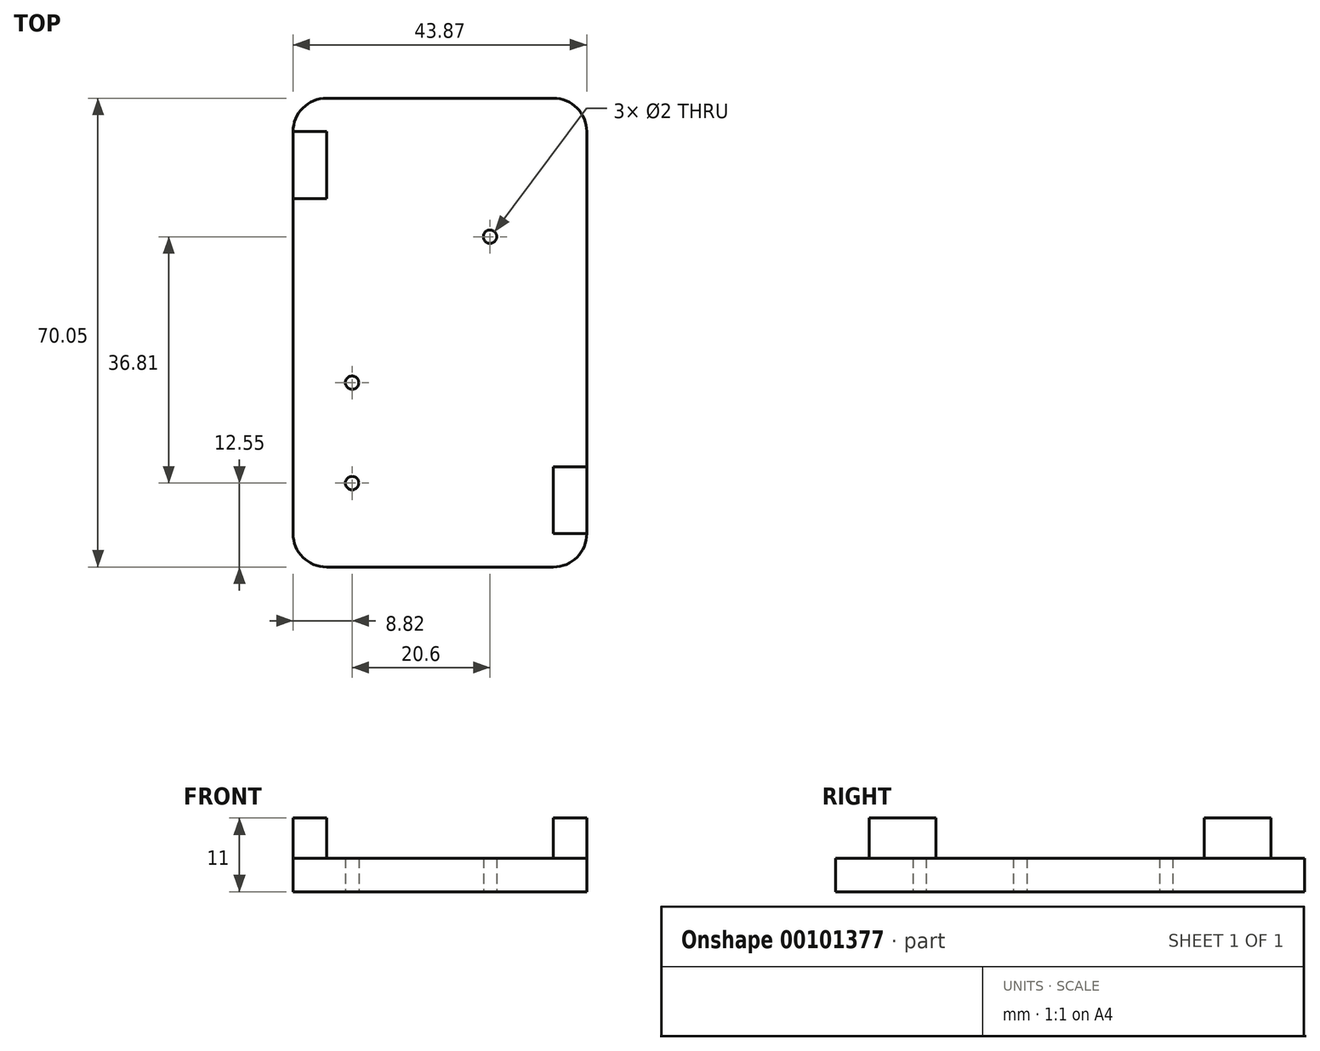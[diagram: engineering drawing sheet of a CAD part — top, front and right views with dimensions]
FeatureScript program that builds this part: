
annotation { "Feature Type Name" : "Feature", "Feature Type Description" : "" }
export const myFeature = defineFeature(function(context is Context, id is Id, definition is map)
    precondition{}
    {
        {
            var Q0;
            Q0=qCreatedBy(makeId("Top.planeOp"),FACE);
            var sketch = newSketch(context, id + "F0", { "sketchPlane" : qUnion([Q0])});
            skLineSegment(sketch, "E0", {"start": v(5, 0) * mm, "end": v(38.87, 0) * mm});
            skLineSegment(sketch, "E1", {"start": v(0, 5) * mm, "end": v(0, 65.05) * mm});
            skLineSegment(sketch, "E2", {"start": v(5, 70.05) * mm, "end": v(38.87, 70.05) * mm});
            skLineSegment(sketch, "E3", {"start": v(43.87, 65.05) * mm, "end": v(43.87, 5) * mm});
            skPoint(sketch, "E4.visualSharp", {"position": v(0, 70.05) * mm});
            skArc(sketch, "E4.filletArc", {"start": v(5, 70.05) * mm, "mid": v(1.46, 68.59) * mm, "end": v(0, 65.05) * mm});
            skPoint(sketch, "E5.visualSharp", {"position": v(43.87, 70.05) * mm});
            skArc(sketch, "E5.filletArc", {"start": v(43.87, 65.05) * mm, "mid": v(42.4, 68.59) * mm, "end": v(38.87, 70.05) * mm});
            skPoint(sketch, "E6.visualSharp", {"position": v(43.87, 0) * mm});
            skArc(sketch, "E6.filletArc", {"start": v(38.87, 0) * mm, "mid": v(42.4, 1.46) * mm, "end": v(43.87, 5) * mm});
            skPoint(sketch, "E7.visualSharp", {"position": v(0, 0) * mm});
            skArc(sketch, "E7.filletArc", {"start": v(0, 5) * mm, "mid": v(1.46, 1.46) * mm, "end": v(5, 0) * mm});
            skLineSegment(sketch, "E8", {"start": v(43.87, 70.05) * mm, "end": v(43.87, 49.36) * mm});
            skLineSegment(sketch, "E9", {"start": v(43.87, 49.36) * mm, "end": v(29.42, 49.36) * mm});
            skCircle(sketch, "E10", {"center": v(29.42, 49.36) * mm, "radius": 1 * mm});
            skLineSegment(sketch, "E11", {"start": v(29.42, 49.36) * mm, "end": v(8.82, 49.36) * mm});
            skLineSegment(sketch, "E12", {"start": v(8.82, 49.36) * mm, "end": v(8.82, 27.55) * mm});
            skCircle(sketch, "E13", {"center": v(8.82, 27.55) * mm, "radius": 1 * mm});
            skLineSegment(sketch, "E14", {"start": v(8.82, 27.55) * mm, "end": v(8.82, 12.55) * mm});
            skCircle(sketch, "E15", {"center": v(8.82, 12.55) * mm, "radius": 1 * mm});
            skSolve(sketch);
        }
        {
            var Q0;
            Q0=makeQuery(id+"F0.imprint","IMPRINT",FACE,{"disambiguationData":[TD([[makeQuery(id+"F0.imprint","IMPRINT",EDGE,{"derivedFrom":sQuery(id+"F0.wireOp",EDGE,"E0")}),1.0]])]});
            extrude(context, id + "F1", {"entities" : qUnion([Q0]), "depth" : 5 * mm});
        }
        {
            var Q0;
            Q0=makeQuery(id+"F1.opExtrude","CAP_FACE",FACE,{"disambiguationData":[OSD([sQuery(id+"F0.wireOp",EDGE,"E0"),sQuery(id+"F0.wireOp",EDGE,"E1"),sQuery(id+"F0.wireOp",EDGE,"E2"),sQuery(id+"F0.wireOp",EDGE,"E3"),sQuery(id+"F0.wireOp",EDGE,"E4.filletArc"),sQuery(id+"F0.wireOp",EDGE,"E5.filletArc"),sQuery(id+"F0.wireOp",EDGE,"E6.filletArc"),sQuery(id+"F0.wireOp",EDGE,"E7.filletArc"),sQuery(id+"F0.wireOp",EDGE,"E8"),sQuery(id+"F0.wireOp",EDGE,"E10"),sQuery(id+"F0.wireOp",EDGE,"E13"),sQuery(id+"F0.wireOp",EDGE,"E15")])],"isStart":false});
            var sketch = newSketch(context, id + "F2", { "sketchPlane" : qUnion([Q0])});
            skLineSegment(sketch, "E16.bottom", {"start": v(0, 65.05) * mm, "end": v(5, 65.05) * mm});
            skLineSegment(sketch, "E16.top", {"start": v(0, 55.05) * mm, "end": v(5, 55.05) * mm});
            skLineSegment(sketch, "E16.left", {"start": v(0, 65.05) * mm, "end": v(0, 55.05) * mm});
            skLineSegment(sketch, "E16.right", {"start": v(5, 65.05) * mm, "end": v(5, 55.05) * mm});
            skLineSegment(sketch, "E17.bottom", {"start": v(43.87, 5) * mm, "end": v(38.87, 5) * mm});
            skLineSegment(sketch, "E17.top", {"start": v(43.87, 15) * mm, "end": v(38.87, 15) * mm});
            skLineSegment(sketch, "E17.left", {"start": v(43.87, 5) * mm, "end": v(43.87, 15) * mm});
            skLineSegment(sketch, "E17.right", {"start": v(38.87, 5) * mm, "end": v(38.87, 15) * mm});
            skLineSegment(sketch, "E18.bottom", {"start": v(38.87, 0) * mm, "end": v(28.87, 0) * mm});
            skLineSegment(sketch, "E18.top", {"start": v(38.87, 5) * mm, "end": v(28.87, 5) * mm});
            skLineSegment(sketch, "E18.left", {"start": v(38.87, 0) * mm, "end": v(38.87, 5) * mm});
            skLineSegment(sketch, "E18.right", {"start": v(28.87, 0) * mm, "end": v(28.87, 5) * mm});
            skSolve(sketch);
        }
        {
            var Q0;
            Q0=makeQuery(id+"F2.imprint","IMPRINT",FACE,{"disambiguationData":[TD([[makeQuery(id+"F2.imprint","IMPRINT",EDGE,{"derivedFrom":sQuery(id+"F2.wireOp",EDGE,"E18.bottom")}),1.0]])]});
            var Q1;
            Q1=makeQuery(id+"F2.imprint","IMPRINT",FACE,{"disambiguationData":[TD([[makeQuery(id+"F2.imprint","IMPRINT",EDGE,{"derivedFrom":sQuery(id+"F2.wireOp",EDGE,"E17.bottom")}),-1.0]])]});
            var Q2;
            Q2=makeQuery(id+"F2.imprint","IMPRINT",FACE,{"disambiguationData":[TD([[makeQuery(id+"F2.imprint","IMPRINT",EDGE,{"derivedFrom":sQuery(id+"F2.wireOp",EDGE,"E16.bottom")}),-1.0]])]});
            extrude(context, id + "F3", {"entities" : qUnion([Q0, Q1, Q2]), "depth" : 6 * mm});
        }
        {
            var Q0;
            Q0=makeQuery(id+"F3.opExtrude","SWEPT_BODY",BODY,{"disambiguationData":[OSD([sQuery(id+"F2.wireOp",EDGE,"E18.bottom"),sQuery(id+"F2.wireOp",EDGE,"E18.top"),sQuery(id+"F2.wireOp",EDGE,"E18.left"),sQuery(id+"F2.wireOp",EDGE,"E18.right")])]});
            deleteBodies(context, id + "F4", {"entities" : qUnion([Q0])});
        }
    });
